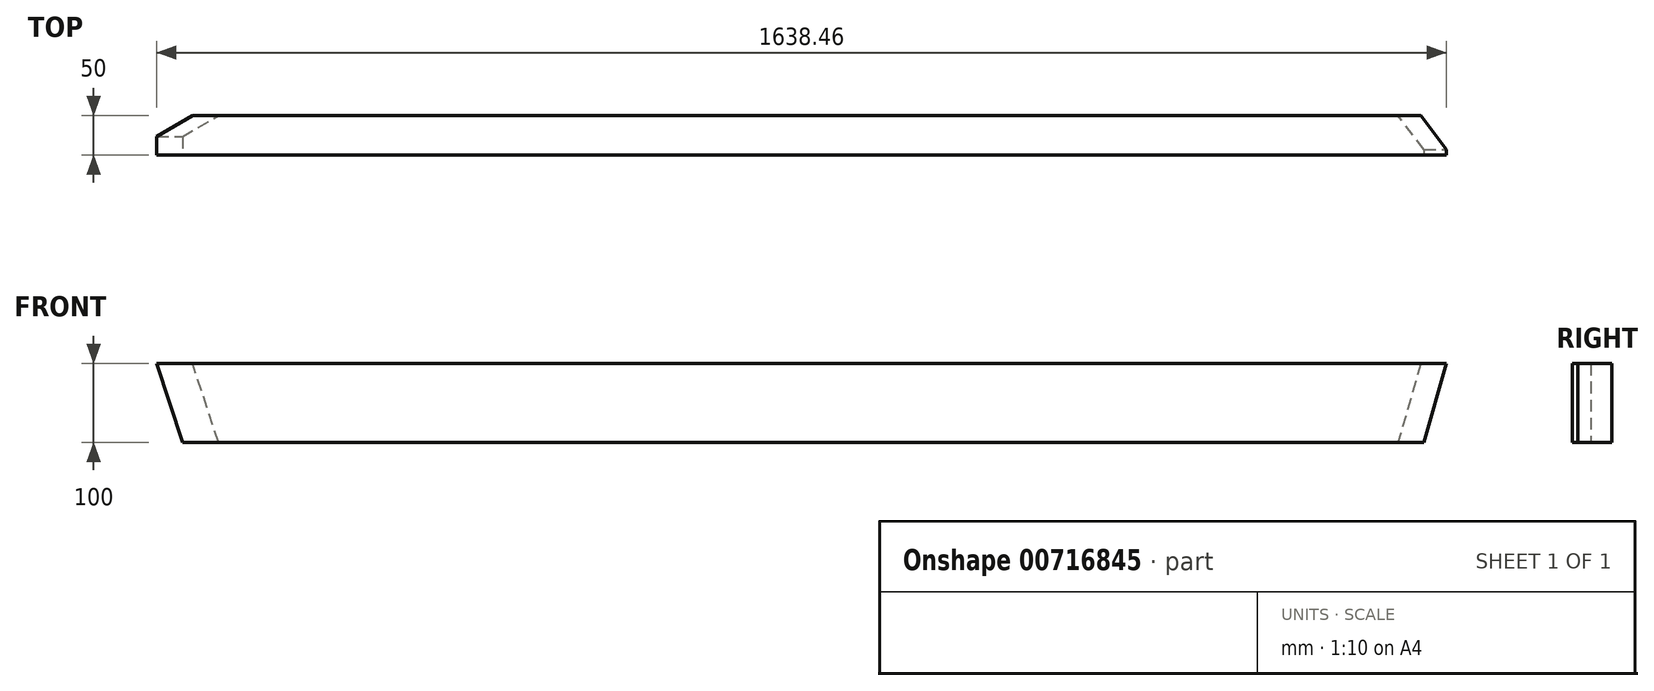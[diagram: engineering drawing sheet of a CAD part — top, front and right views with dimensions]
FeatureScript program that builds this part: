
annotation { "Feature Type Name" : "Feature", "Feature Type Description" : "" }
export const myFeature = defineFeature(function(context is Context, id is Id, definition is map)
    precondition{}
    {
        {
            var Q0;
            Q0=qCreatedBy(makeId("Right.planeOp"),FACE);
            var sketch = newSketch(context, id + "F0", { "sketchPlane" : qUnion([Q0])});
            skLineSegment(sketch, "E0.bottom", {"start": v(-25, -50) * mm, "end": v(25, -50) * mm});
            skLineSegment(sketch, "E0.top", {"start": v(-25, 50) * mm, "end": v(25, 50) * mm});
            skLineSegment(sketch, "E0.left", {"start": v(-25, -50) * mm, "end": v(-25, 50) * mm});
            skLineSegment(sketch, "E0.right", {"start": v(25, -50) * mm, "end": v(25, 50) * mm});
            skPoint(sketch, "E0.middle", {"position": v(0, 0) * mm});
            skSolve(sketch);
        }
        {
            var Q0;
            Q0=makeQuery(id+"F0.imprint","IMPRINT",FACE,{"disambiguationData":[TD([[makeQuery(id+"F0.imprint","IMPRINT",EDGE,{"derivedFrom":sQuery(id+"F0.wireOp",EDGE,"E0.bottom")}),1.0]])]});
            extrude(context, id + "F1", {"entities" : qUnion([Q0]), "endBound" : BoundingType.SYMMETRIC, "depth" : 1638.45 * mm, "offsetDistance" : 25 * mm});
        }
        {
            var Q0;
            Q0=makeQuery(id+"F1.opExtrude","SWEPT_FACE",FACE,{"disambiguationData":[OSD([sQuery(id+"F0.wireOp",EDGE,"E0.left")])]});
            var sketch = newSketch(context, id + "F2", { "sketchPlane" : qUnion([Q0])});
            skLineSegment(sketch, "E1", {"start": v(-819.23, 50) * mm, "end": v(-786.15, -50) * mm});
            skLineSegment(sketch, "E2", {"start": v(819.23, 50) * mm, "end": v(790.55, -50) * mm});
            skSolve(sketch);
        }
        {
            var Q0;
            {var subQ0=sQuery(id+"F2.wireOp",EDGE,"E2");Q0=makeQuery(id+"F2.imprint","IMPRINT",FACE,{"disambiguationData":[TD([[makeQuery(id+"F2.imprint","IMPRINT",EDGE,{"derivedFrom":subQ0}),1.0]])]});}
            var Q1;
            {var subQ0=sQuery(id+"F2.wireOp",EDGE,"E1");Q1=makeQuery(id+"F2.imprint","IMPRINT",FACE,{"disambiguationData":[TD([[makeQuery(id+"F2.imprint","IMPRINT",EDGE,{"derivedFrom":subQ0}),-1.0]])]});}
            extrude(context, id + "F3", {"entities" : qUnion([Q0, Q1]), "operationType" : NewBodyOperationType.REMOVE, "endBound" : BoundingType.THROUGH_ALL, "oppositeDirection" : true, "depth" : 25 * mm, "offsetDistance" : 25 * mm});
        }
        {
            var Q0;
            Q0=makeQuery(id+"F3.boolean.opBoolean","COPY",EDGE,{"derivedFrom":makeQuery(id+"F3.opExtrude","CAP_EDGE",EDGE,{"disambiguationData":[OSD([sQuery(id+"F2.wireOp",EDGE,"E2")])],"isStart":true})});
            var Q1;
            Q1=makeQuery(id+"F3.boolean.opBoolean","INTERSECT",EDGE,{"derivedFrom":[makeQuery(id+"F1.opExtrude","SWEPT_FACE",FACE,{"disambiguationData":[OSD([sQuery(id+"F0.wireOp",EDGE,"E0.right")])]}),makeQuery(id+"F3.opExtrude","SWEPT_FACE",FACE,{"disambiguationData":[OSD([sQuery(id+"F2.wireOp",EDGE,"E2")])]})]});
            chamfer(context, id + "F4", {"entities" : qUnion([Q0, Q1]), "chamferType" : ChamferType.OFFSET_ANGLE, "width" : 43.3 * mm, "oppositeDirection" : true, "angle" : 36 * degree, "tangentPropagation" : true});
        }
        {
            var Q0;
            Q0=makeQuery(id+"F3.boolean.opBoolean","INTERSECT",EDGE,{"derivedFrom":[makeQuery(id+"F1.opExtrude","SWEPT_FACE",FACE,{"disambiguationData":[OSD([sQuery(id+"F0.wireOp",EDGE,"E0.right")])]}),makeQuery(id+"F3.opExtrude","SWEPT_FACE",FACE,{"disambiguationData":[OSD([sQuery(id+"F2.wireOp",EDGE,"E1")])]})]});
            var Q1;
            Q1=makeQuery(id+"F3.boolean.opBoolean","COPY",EDGE,{"derivedFrom":makeQuery(id+"F3.opExtrude","CAP_EDGE",EDGE,{"disambiguationData":[OSD([sQuery(id+"F2.wireOp",EDGE,"E1")])],"isStart":true})});
            chamfer(context, id + "F5", {"entities" : qUnion([Q0, Q1]), "chamferType" : ChamferType.OFFSET_ANGLE, "width" : 43.3 * mm, "oppositeDirection" : true, "angle" : 31.68 * degree, "tangentPropagation" : true});
        }
    });
